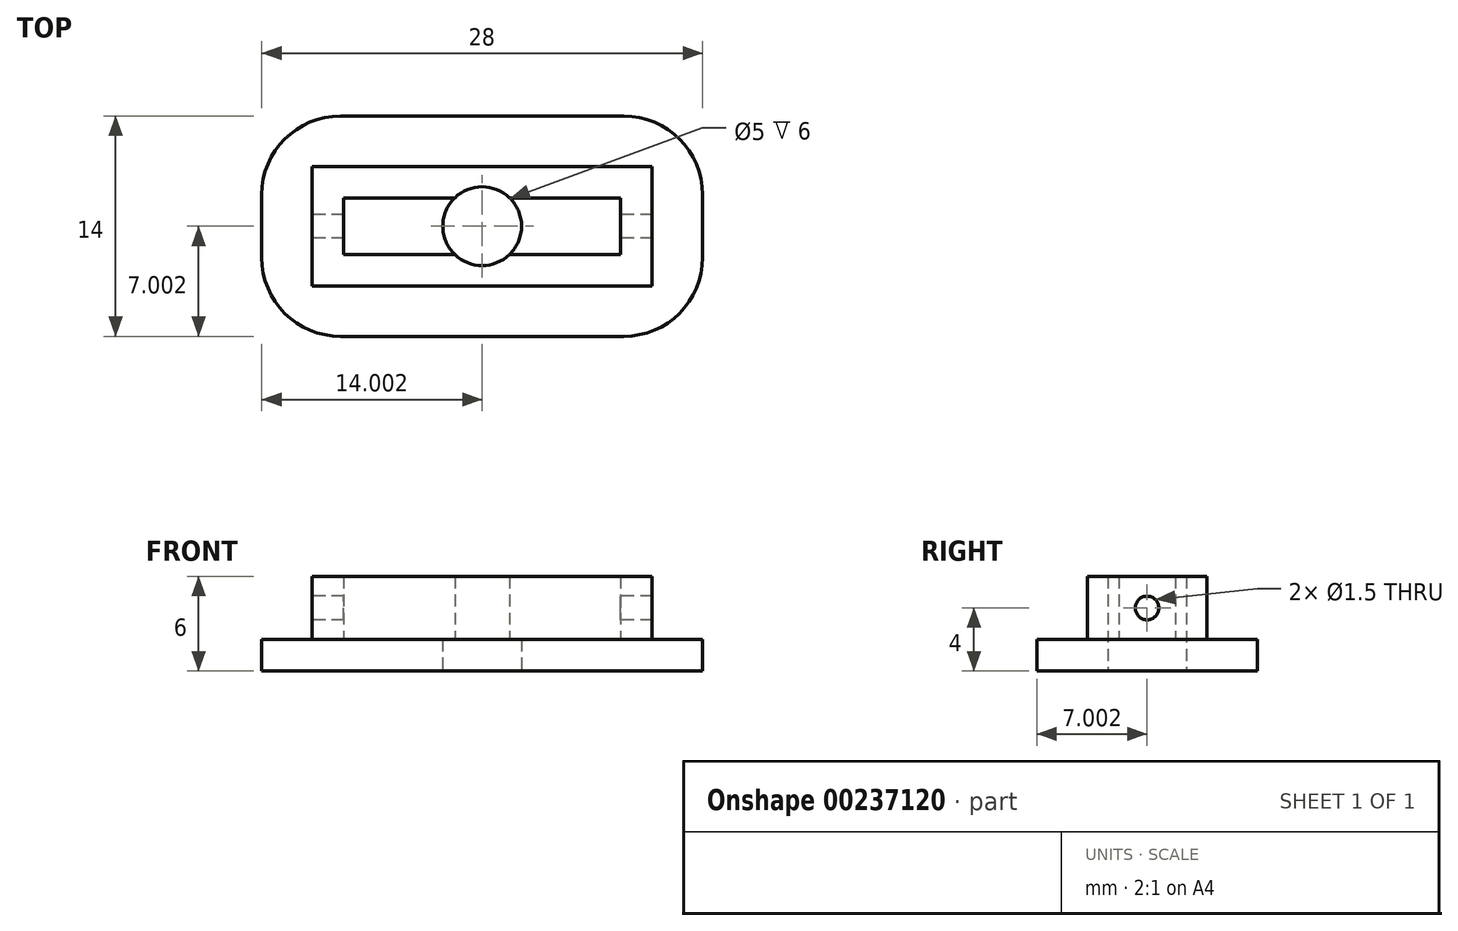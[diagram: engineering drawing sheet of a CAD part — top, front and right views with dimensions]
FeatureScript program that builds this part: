
annotation { "Feature Type Name" : "Feature", "Feature Type Description" : "" }
export const myFeature = defineFeature(function(context is Context, id is Id, definition is map)
    precondition{}
    {
        {
            var Q0;
            Q0=qCreatedBy(makeId("Top.planeOp"),FACE);
            var sketch = newSketch(context, id + "F0", { "sketchPlane" : qUnion([Q0])});
            skLineSegment(sketch, "E0.0", {"start": v(14.55, 9.25) * mm, "end": v(14.55, 1.25) * mm});
            skLineSegment(sketch, "E0.1", {"start": v(14.55, 1.25) * mm, "end": v(-7.45, 1.25) * mm});
            skLineSegment(sketch, "E0.2", {"start": v(14.55, 9.25) * mm, "end": v(-7.45, 9.25) * mm});
            skLineSegment(sketch, "E0.3", {"start": v(-7.45, 9.25) * mm, "end": v(-7.45, 1.25) * mm});
            skLineSegment(sketch, "E1.0", {"start": v(17.55, 7.25) * mm, "end": v(17.55, 3.25) * mm});
            skLineSegment(sketch, "E1.1", {"start": v(12.55, 12.25) * mm, "end": v(-5.45, 12.25) * mm});
            skLineSegment(sketch, "E1.2", {"start": v(-10.45, 7.25) * mm, "end": v(-10.45, 3.25) * mm});
            skLineSegment(sketch, "E1.3", {"start": v(12.55, -1.75) * mm, "end": v(-5.45, -1.75) * mm});
            skPoint(sketch, "E2.visualSharp", {"position": v(17.55, 12.25) * mm});
            skArc(sketch, "E2.filletArc", {"start": v(17.55, 7.25) * mm, "mid": v(16.09, 10.79) * mm, "end": v(12.55, 12.25) * mm});
            skPoint(sketch, "E3.visualSharp", {"position": v(17.55, -1.75) * mm});
            skArc(sketch, "E3.filletArc", {"start": v(12.55, -1.75) * mm, "mid": v(16.09, -0.28) * mm, "end": v(17.55, 3.25) * mm});
            skPoint(sketch, "E4.visualSharp", {"position": v(-10.45, -1.75) * mm});
            skArc(sketch, "E4.filletArc", {"start": v(-10.45, 3.25) * mm, "mid": v(-8.98, -0.28) * mm, "end": v(-5.45, -1.75) * mm});
            skPoint(sketch, "E5.visualSharp", {"position": v(-10.45, 12.25) * mm});
            skArc(sketch, "E5.filletArc", {"start": v(-5.45, 12.25) * mm, "mid": v(-8.98, 10.79) * mm, "end": v(-10.45, 7.25) * mm});
            skLineSegment(sketch, "E6.0", {"start": v(14.35, 9.05) * mm, "end": v(-7.25, 9.05) * mm});
            skLineSegment(sketch, "E6.1", {"start": v(14.35, 9.05) * mm, "end": v(14.35, 1.45) * mm});
            skLineSegment(sketch, "E6.2", {"start": v(14.35, 1.45) * mm, "end": v(-7.25, 1.45) * mm});
            skLineSegment(sketch, "E6.3", {"start": v(-7.25, 9.05) * mm, "end": v(-7.25, 1.45) * mm});
            skLineSegment(sketch, "E7.0", {"start": v(12.35, 7.05) * mm, "end": v(-5.25, 7.05) * mm});
            skLineSegment(sketch, "E7.1", {"start": v(12.35, 7.05) * mm, "end": v(12.35, 3.45) * mm});
            skLineSegment(sketch, "E7.2", {"start": v(12.35, 3.45) * mm, "end": v(-5.25, 3.45) * mm});
            skLineSegment(sketch, "E7.3", {"start": v(-5.25, 7.05) * mm, "end": v(-5.25, 3.45) * mm});
            skSolve(sketch);
        }
        {
            var Q0;
            Q0=makeQuery(id+"F0.imprint","IMPRINT",FACE,{"disambiguationData":[TD([[makeQuery(id+"F0.imprint","IMPRINT",EDGE,{"derivedFrom":sQuery(id+"F0.wireOp",EDGE,"E0.0")}),1.0]])]});
            var Q1;
            Q1=makeQuery(id+"F0.imprint","IMPRINT",FACE,{"disambiguationData":[TD([[makeQuery(id+"F0.imprint","IMPRINT",EDGE,{"derivedFrom":sQuery(id+"F0.wireOp",EDGE,"E7.0")}),1.0]])]});
            var Q2;
            Q2=makeQuery(id+"F0.imprint","IMPRINT",FACE,{"disambiguationData":[TD([[makeQuery(id+"F0.imprint","IMPRINT",EDGE,{"derivedFrom":sQuery(id+"F0.wireOp",EDGE,"E0.0")}),-1.0]])]});
            var Q3;
            Q3=makeQuery(id+"F0.imprint","IMPRINT",FACE,{"disambiguationData":[TD([[makeQuery(id+"F0.imprint","IMPRINT",EDGE,{"derivedFrom":sQuery(id+"F0.wireOp",EDGE,"E6.0")}),1.0]])]});
            extrude(context, id + "F1", {"entities" : qUnion([Q0, Q1, Q2, Q3]), "oppositeDirection" : true, "depth" : 2 * mm});
        }
        {
            var Q0;
            Q0=makeQuery(id+"F0.imprint","IMPRINT",FACE,{"disambiguationData":[TD([[makeQuery(id+"F0.imprint","IMPRINT",EDGE,{"derivedFrom":sQuery(id+"F0.wireOp",EDGE,"E6.0")}),1.0]])]});
            extrude(context, id + "F2", {"entities" : qUnion([Q0]), "operationType" : NewBodyOperationType.ADD, "depth" : 4 * mm});
        }
        {
            var Q0;
            Q0=makeQuery(id+"F1.opExtrude","CAP_FACE",FACE,{"disambiguationData":[OSD([sQuery(id+"F0.wireOp",EDGE,"E1.0"),sQuery(id+"F0.wireOp",EDGE,"E1.1"),sQuery(id+"F0.wireOp",EDGE,"E1.2"),sQuery(id+"F0.wireOp",EDGE,"E1.3"),sQuery(id+"F0.wireOp",EDGE,"E2.filletArc"),sQuery(id+"F0.wireOp",EDGE,"E3.filletArc"),sQuery(id+"F0.wireOp",EDGE,"E4.filletArc"),sQuery(id+"F0.wireOp",EDGE,"E5.filletArc")])],"isStart":false});
            var sketch = newSketch(context, id + "F3", { "sketchPlane" : qUnion([Q0])});
            skLineSegment(sketch, "E8.0", {"start": v(-5.25, -7.05) * mm, "end": v(-5.25, -3.45) * mm, "construction": true});
            skLineSegment(sketch, "E8.1", {"start": v(12.35, -7.05) * mm, "end": v(12.35, -3.45) * mm, "construction": true});
            skLineSegment(sketch, "E9", {"start": v(-5.25, -5.25) * mm, "end": v(12.35, -5.25) * mm, "construction": true});
            skCircle(sketch, "E10", {"center": v(3.55, -5.25) * mm, "radius": 2.5 * mm});
            skSolve(sketch);
        }
        {
            var Q0;
            Q0=makeQuery(id+"F3.imprint","IMPRINT",FACE,{"disambiguationData":[TD([[makeQuery(id+"F3.imprint","IMPRINT",EDGE,{"derivedFrom":sQuery(id+"F3.wireOp",EDGE,"E10")}),1.0]])]});
            extrude(context, id + "F4", {"entities" : qUnion([Q0]), "operationType" : NewBodyOperationType.REMOVE, "oppositeDirection" : true, "depth" : 10 * mm, "hasSecondDirection" : true, "secondDirectionOppositeDirection" : false, "secondDirectionDepth" : 10 * mm});
        }
        {
            var Q0;
            Q0=makeQuery(id+"F2.opExtrude","SWEPT_FACE",FACE,{"disambiguationData":[OSD([sQuery(id+"F0.wireOp",EDGE,"E6.3")])]});
            var sketch = newSketch(context, id + "F5", { "sketchPlane" : qUnion([Q0])});
            skCircle(sketch, "E11", {"center": v(-5.25, 2) * mm, "radius": 0.75 * mm});
            skPoint(sketch, "E11.centerSnap0", {"position": v(-5.25, 0) * mm});
            skSolve(sketch);
        }
        {
            var Q0;
            Q0=makeQuery(id+"F5.imprint","IMPRINT",FACE,{"disambiguationData":[TD([[makeQuery(id+"F5.imprint","IMPRINT",EDGE,{"derivedFrom":sQuery(id+"F5.wireOp",EDGE,"E11")}),1.0]])]});
            var Q1;
            Q1=sQuery(id+"F5.wireOp",EDGE,"1UgINDJq-5C1f-MJd3-aRPC-EX84uS9XgLad");
            extrude(context, id + "F6", {"entities" : qUnion([Q0]), "operationType" : NewBodyOperationType.REMOVE, "surfaceEntities" : qUnion([Q1]), "endBound" : BoundingType.THROUGH_ALL, "oppositeDirection" : true, "depth" : 25 * mm, "hasSecondDirection" : true, "secondDirectionBound" : SecondDirectionBoundingType.THROUGH_ALL, "secondDirectionOppositeDirection" : false, "secondDirectionDepth" : 25 * mm});
        }
    });
